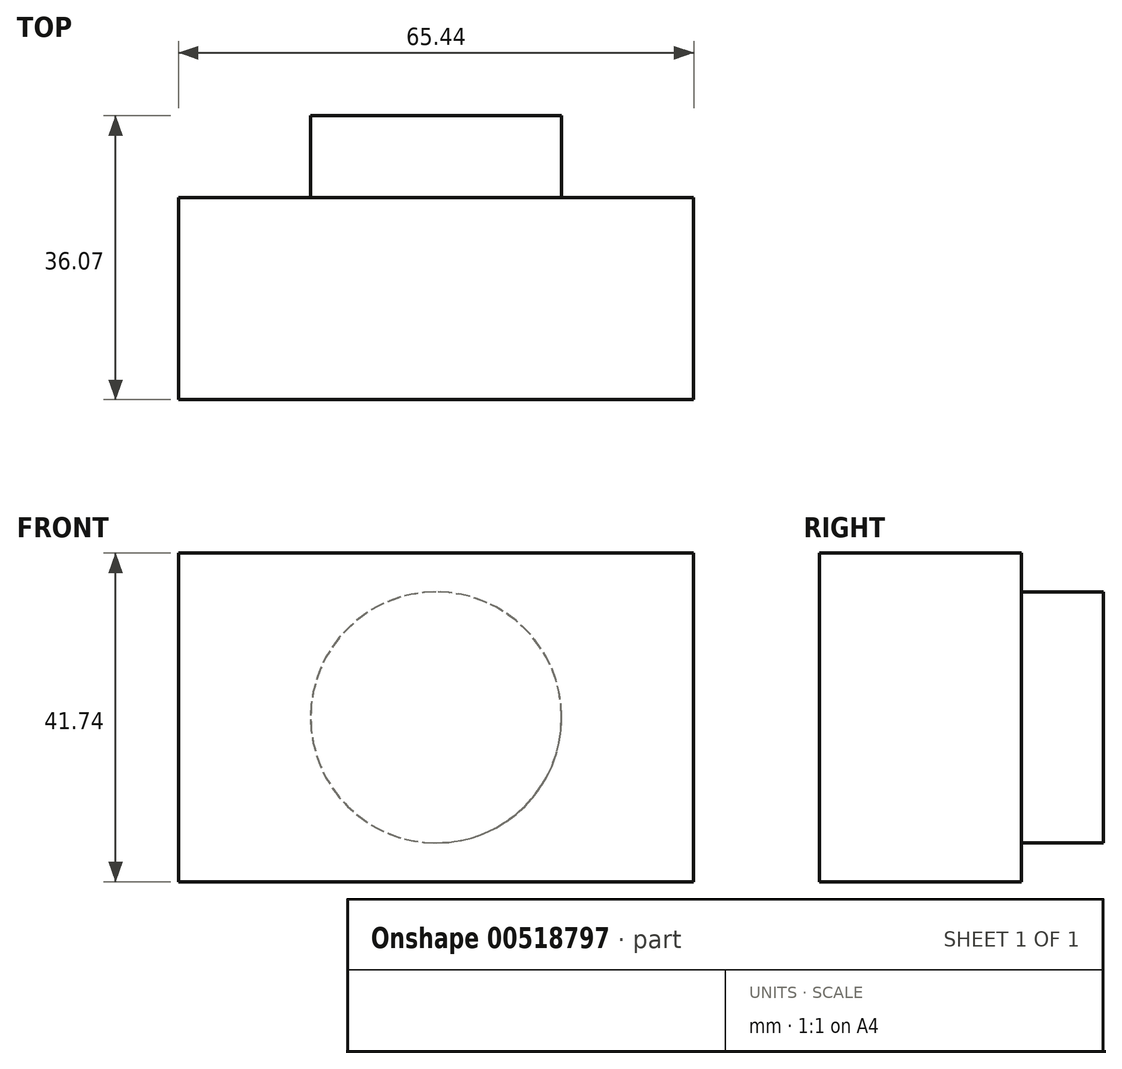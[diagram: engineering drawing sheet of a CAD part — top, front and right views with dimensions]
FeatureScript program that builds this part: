
annotation { "Feature Type Name" : "Feature", "Feature Type Description" : "" }
export const myFeature = defineFeature(function(context is Context, id is Id, definition is map)
    precondition{}
    {
        {
            var Q0;
            Q0=qCreatedBy(makeId("Front.planeOp"),FACE);
            var sketch = newSketch(context, id + "F0", { "sketchPlane" : qUnion([Q0])});
            skLineSegment(sketch, "E0.bottom", {"start": v(32.72, 20.87) * mm, "end": v(-32.72, 20.87) * mm});
            skLineSegment(sketch, "E0.top", {"start": v(32.72, -20.87) * mm, "end": v(-32.72, -20.87) * mm});
            skLineSegment(sketch, "E0.left", {"start": v(32.72, 20.87) * mm, "end": v(32.72, -20.87) * mm});
            skLineSegment(sketch, "E0.right", {"start": v(-32.72, 20.87) * mm, "end": v(-32.72, -20.87) * mm});
            skPoint(sketch, "E0.middle", {"position": v(0, 0) * mm});
            skSolve(sketch);
        }
        {
            var Q0;
            Q0=makeQuery(id+"F0.imprint","IMPRINT",FACE,{"disambiguationData":[TD([[makeQuery(id+"F0.imprint","IMPRINT",EDGE,{"derivedFrom":sQuery(id+"F0.wireOp",EDGE,"E0.bottom")}),1.0]])]});
            extrude(context, id + "F1", {"entities" : qUnion([Q0]), "depth" : 25.4 * mm});
        }
        {
            var Q0;
            Q0=makeQuery(id+"F1.opExtrude","CAP_FACE",FACE,{"disambiguationData":[OSD([sQuery(id+"F0.wireOp",EDGE,"E0.bottom"),sQuery(id+"F0.wireOp",EDGE,"E0.top"),sQuery(id+"F0.wireOp",EDGE,"E0.left"),sQuery(id+"F0.wireOp",EDGE,"E0.right")])],"isStart":true});
            var sketch = newSketch(context, id + "F2", { "sketchPlane" : qUnion([Q0])});
            skCircle(sketch, "E1", {"center": v(0, 0) * mm, "radius": 15.94 * mm});
            skSolve(sketch);
        }
        {
            var Q0;
            Q0=makeQuery(id+"F2.imprint","IMPRINT",FACE,{"disambiguationData":[TD([[makeQuery(id+"F2.imprint","IMPRINT",EDGE,{"derivedFrom":sQuery(id+"F2.wireOp",EDGE,"E1")}),1.0]])]});
            extrude(context, id + "F3", {"entities" : qUnion([Q0]), "operationType" : NewBodyOperationType.ADD, "depth" : 7.37 * mm});
        }
        {
            var Q0;
            Q0=makeQuery(id+"F1.opExtrude","CAP_FACE",FACE,{"disambiguationData":[OSD([sQuery(id+"F0.wireOp",EDGE,"E0.bottom"),sQuery(id+"F0.wireOp",EDGE,"E0.top"),sQuery(id+"F0.wireOp",EDGE,"E0.left"),sQuery(id+"F0.wireOp",EDGE,"E0.right")])],"isStart":true});
            extrude(context, id + "F4", {"entities" : qUnion([Q0]), "operationType" : NewBodyOperationType.ADD, "depth" : 0.25 * mm});
        }
        {
            var Q0;
            Q0=makeQuery(id+"F3.opExtrude","CAP_FACE",FACE,{"disambiguationData":[OSD([sQuery(id+"F2.wireOp",EDGE,"E1")])],"isStart":false});
            extrude(context, id + "F5", {"entities" : qUnion([Q0]), "operationType" : NewBodyOperationType.ADD, "depth" : 3.3 * mm});
        }
    });
